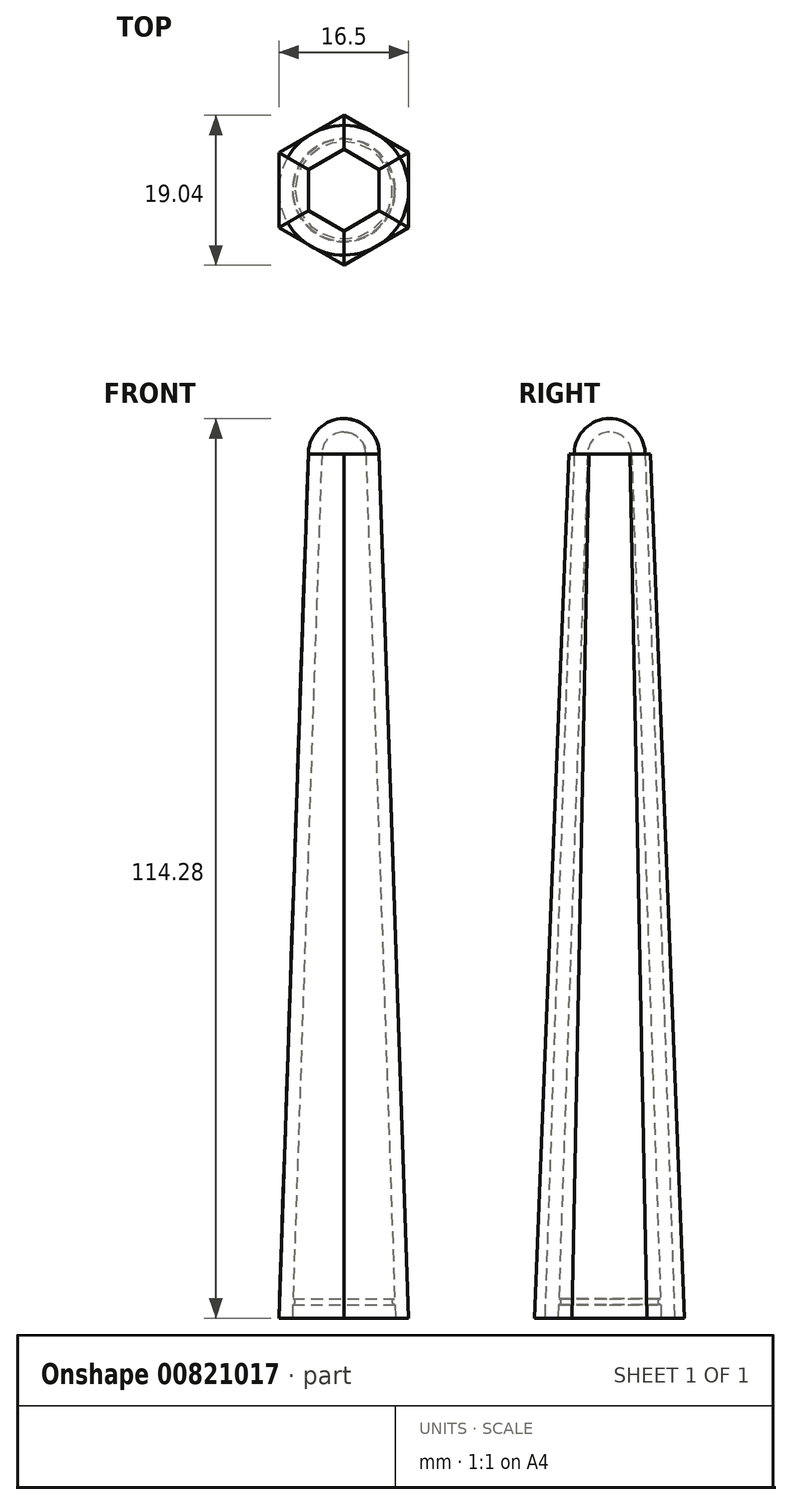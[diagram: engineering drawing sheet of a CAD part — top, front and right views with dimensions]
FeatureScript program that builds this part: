
annotation { "Feature Type Name" : "Feature", "Feature Type Description" : "" }
export const myFeature = defineFeature(function(context is Context, id is Id, definition is map)
    precondition{}
    {
        {
            var Q0;
            Q0=qCreatedBy(makeId("Front.planeOp"),FACE);
            var sketch = newSketch(context, id + "F0", { "sketchPlane" : qUnion([Q0])});
            skArc(sketch, "E0", {"start": v(4.5, 0.15) * mm, "mid": v(3.13, 3.24) * mm, "end": v(0, 4.5) * mm});
            skLineSegment(sketch, "E1", {"start": v(4.5, 0.15) * mm, "end": v(8.25, -109.78) * mm});
            skPoint(sketch, "E2", {"position": v(0, 4.5) * mm});
            skLineSegment(sketch, "E3", {"start": v(6.54, -109.78) * mm, "end": v(2.8, 0.1) * mm});
            skPoint(sketch, "E4", {"position": v(0, 2.8) * mm});
            skArc(sketch, "E5", {"start": v(2.8, 0.1) * mm, "mid": v(1.95, 2.01) * mm, "end": v(0, 2.8) * mm});
            skLineSegment(sketch, "E6", {"start": v(2.8, 0.1) * mm, "end": v(0, 0) * mm, "construction": true});
            skLineSegment(sketch, "E7", {"start": v(8.25, -109.78) * mm, "end": v(6.54, -109.78) * mm});
            skPoint(sketch, "E8.center.orphan", {"position": v(0, -110.06) * mm});
            skLineSegment(sketch, "E9", {"start": v(0, 4.5) * mm, "end": v(0, 2.8) * mm});
            skLineSegment(sketch, "E10", {"start": v(0, -110.06) * mm, "end": v(0, 4.5) * mm, "construction": true});
            skPoint(sketch, "E11", {"position": v(6.49, -108.08) * mm});
            skPoint(sketch, "E12", {"position": v(6.46, -107.28) * mm});
            skLineSegment(sketch, "E13", {"start": v(6.49, -108.08) * mm, "end": v(6.49, -108.08) * mm});
            skLineSegment(sketch, "E14", {"start": v(6.46, -107.28) * mm, "end": v(6.46, -107.28) * mm});
            skLineSegment(sketch, "E15", {"start": v(6.49, -108.08) * mm, "end": v(6.46, -107.28) * mm});
            skLineSegment(sketch, "E16", {"start": v(6.49, -108.08) * mm, "end": v(6.5, -108.58) * mm});
            skPoint(sketch, "E17", {"position": v(6.44, -106.78) * mm});
            skPoint(sketch, "E18", {"position": v(6.47, -107.68) * mm});
            skLineSegment(sketch, "E19", {"start": v(6.17, -107.68) * mm, "end": v(6.47, -107.68) * mm});
            skArc(sketch, "E20", {"start": v(6.46, -107.28) * mm, "mid": v(6.17, -107.7) * mm, "end": v(6.49, -108.08) * mm});
            skSolve(sketch);
        }
        {
            var Q0;
            Q0=makeQuery(id+"F0.imprint","IMPRINT",FACE,{"disambiguationData":[TD([[makeQuery(id+"F0.imprint","IMPRINT",EDGE,{"derivedFrom":sQuery(id+"F0.wireOp",EDGE,"E0")}),1.0]])]});
            var Q1;
            {var subQ0=sQuery(id+"F0.wireOp",EDGE,"E13");Q1=makeQuery(id+"F0.imprint","IMPRINT",FACE,{"disambiguationData":[TD([[makeQuery(id+"F0.imprint","IMPRINT",EDGE,{"derivedFrom":subQ0}),-1.0]])]});}
            var Q2;
            {var subQ3=sQuery(id+"F0.wireOp",EDGE,"E19");Q2=makeQuery(id+"F0.imprint","IMPRINT",FACE,{"disambiguationData":[TD([[makeQuery(id+"F0.imprint","IMPRINT",EDGE,{"derivedFrom":subQ3}),1.0]])]});}
            var Q3;
            {var subQ3=sQuery(id+"F0.wireOp",EDGE,"E19");Q3=makeQuery(id+"F0.imprint","IMPRINT",FACE,{"disambiguationData":[TD([[makeQuery(id+"F0.imprint","IMPRINT",EDGE,{"derivedFrom":subQ3}),-1.0]])]});}
            var Q4;
            Q4=sQuery(id+"F0.wireOp",EDGE,"E10");
            revolve(context, id + "F1", {"surfaceOperationType" : NewSurfaceOperationType.NEW, "entities" : qUnion([Q0, Q1, Q2, Q3]), "axis" : qUnion([Q4]), "revolveType" : RevolveType.FULL});
        }
        {
            var Q0;
            Q0=makeQuery(id+"F1.opRevolve","SWEPT_FACE",FACE,{"disambiguationData":[OSD([sQuery(id+"F0.wireOp",EDGE,"E7")])]});
            var sketch = newSketch(context, id + "F2", { "sketchPlane" : qUnion([Q0])});
            skCircle(sketch, "E21.cCircle", {"center": v(0, 0) * mm, "radius": 8.25 * mm, "construction": true});
            skLineSegment(sketch, "E21.0", {"start": v(8.25, 4.76) * mm, "end": v(8.25, -4.76) * mm});
            skLineSegment(sketch, "E21.1", {"start": v(8.25, -4.76) * mm, "end": v(0, -9.52) * mm});
            skLineSegment(sketch, "E21.2", {"start": v(0, -9.52) * mm, "end": v(-8.25, -4.76) * mm});
            skLineSegment(sketch, "E21.3", {"start": v(-8.25, -4.76) * mm, "end": v(-8.25, 4.76) * mm});
            skLineSegment(sketch, "E21.4", {"start": v(-8.25, 4.76) * mm, "end": v(0, 9.52) * mm});
            skLineSegment(sketch, "E21.5", {"start": v(0, 9.52) * mm, "end": v(8.25, 4.76) * mm});
            skPoint(sketch, "E21.0.midPoint", {"position": v(8.25, 0) * mm});
            skSolve(sketch);
        }
        {
            var Q0;
            Q0=qCreatedBy(makeId("Top.planeOp"),FACE);
            var sketch = newSketch(context, id + "F3", { "sketchPlane" : qUnion([Q0])});
            skCircle(sketch, "E22.cCircle", {"center": v(0, 0) * mm, "radius": 4.5 * mm, "construction": true});
            skLineSegment(sketch, "E22.0", {"start": v(-4.5, -2.6) * mm, "end": v(-4.5, 2.6) * mm});
            skLineSegment(sketch, "E22.1", {"start": v(-4.5, 2.6) * mm, "end": v(0, 5.2) * mm});
            skLineSegment(sketch, "E22.2", {"start": v(0, 5.2) * mm, "end": v(4.5, 2.6) * mm});
            skLineSegment(sketch, "E22.3", {"start": v(4.5, 2.6) * mm, "end": v(4.5, -2.6) * mm});
            skLineSegment(sketch, "E22.4", {"start": v(4.5, -2.6) * mm, "end": v(0, -5.2) * mm});
            skLineSegment(sketch, "E22.5", {"start": v(0, -5.2) * mm, "end": v(-4.5, -2.6) * mm});
            skPoint(sketch, "E22.0.midPoint", {"position": v(-4.5, 0) * mm});
            skSolve(sketch);
        }
        {
            var Q0;
            Q0 = qSketchRegion(id + "F3", true);
            var Q1;
            Q1 = qSketchRegion(id + "F2", true);
            loft(context, id + "F4", {"sheetProfilesArray" : [{ "sheetProfileEntities" : qUnion([Q0]) }, { "sheetProfileEntities" : qUnion([Q1]) }]});
        }
    });
